# Revit family: BIMON_Котел_Паровой_TEMRON_SL1000
name_source: partatom
category: Оборудование
units: mm (PartAtom-declared; Revit-internal decimal feet)

## family parameters
Всегда вертикально = Да
Классификация = Нет
На основе рабочей плоскости = Нет
Общий = Нет
При загрузке вырезать с полостями = Нет
Размер круглого соединителя = Использовать диаметр
Тип детали = Нормальный
Точка расчета площади = Нет

## types (1)
- BIMON_Котел_Паровой_TEMRON_SL1000
    ADSK_URL страницы изделия = https://temron.ru
    ADSK_Версия Revit = 2019
    ADSK_Версия семейства = 1
    ADSK_Единица измерения = шт
    ADSK_Завод-изготовитель = Temron
    ADSK_Количество = 1
    ADSK_Марка = SL1000
    ADSK_Масса = 2700
    ADSK_Масса_Текст = 2700
    ADSK_Материал = <По категории>
    ADSK_Наименование = Паровой котел для получения насыщенного пара низкого давления Temron SL
    ADSK_Наименование краткое = Паровой котел
    ADSK_Обозначение = SL1000
    DN_Коллектор давления = 32 мм
    DN_Отвод конденсата дымовых газов = 19 мм
    DN_Пар = 50 мм
    DN_Переодическая продувка воды = 32 мм
    DN_Питательная вода = 25 мм
    DN_Постоянная продувка воды = 20 мм
    DN_Предохранительный клапан = 25 мм
    DN_Угодящие газы = 490 мм
    DN_Электрод уровня воды 1 = 125 мм
    DN_Электрод уровня воды 2 = 50 мм
    TEMRON_Емкость котла = 2,15 (1,2/0,95) м³
    TEMRON_Максимальная температура пара = 185 мм
    TEMRON_Максимальное рабочее давление = 1 МПа
    TEMRON_Номинальная производительность = 1000 кг/ч
    TEMRON_Номинальная тепловая мощность котла = 683 кВт
    TEMRON_Номинальная тепловая мощность топки = 807 кВт
    TEMRON_Расход топлива для природного газа = 76 м³/ч
    TEMRON_Сопротивление газового тракта = 3 мбар
    TEMRON_Температура питательной воды = 105 °С
    TEMRON_Температура уходящих газов = 200 °С
    URL = https://temron.ru
    Изготовитель = Temron
    Разработчик = BIMON
    Разработчик_Сайт = https://www.bimon.ru
